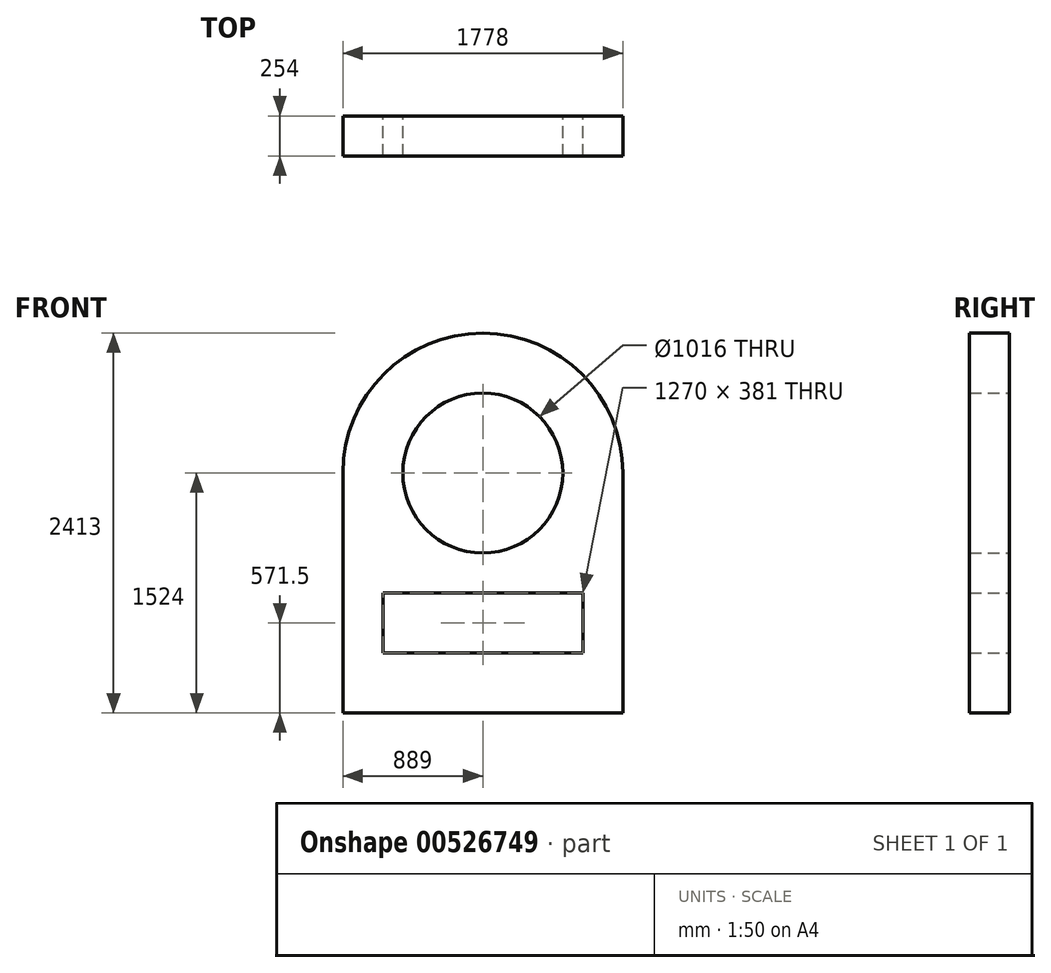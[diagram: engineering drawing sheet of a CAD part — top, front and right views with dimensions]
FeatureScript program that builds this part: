
annotation { "Feature Type Name" : "Feature", "Feature Type Description" : "" }
export const myFeature = defineFeature(function(context is Context, id is Id, definition is map)
    precondition{}
    {
        {
            var Q0;
            Q0=qCreatedBy(makeId("Front.planeOp"),FACE);
            var sketch = newSketch(context, id + "F0", { "sketchPlane" : qUnion([Q0])});
            skLineSegment(sketch, "E0", {"start": v(0, 0) * mm, "end": v(1778, 0) * mm});
            skLineSegment(sketch, "E1", {"start": v(1778, 0) * mm, "end": v(1778, 1524) * mm});
            skLineSegment(sketch, "E2", {"start": v(0, 1524) * mm, "end": v(0, 0) * mm});
            skLineSegment(sketch, "E3", {"start": v(254, 762) * mm, "end": v(254, 381) * mm});
            skLineSegment(sketch, "E4", {"start": v(254, 381) * mm, "end": v(1524, 381) * mm});
            skLineSegment(sketch, "E5", {"start": v(1524, 381) * mm, "end": v(1524, 762) * mm});
            skLineSegment(sketch, "E6", {"start": v(1524, 762) * mm, "end": v(254, 762) * mm});
            skArc(sketch, "E7", {"start": v(1778, 1524) * mm, "mid": v(889, 2413) * mm, "end": v(0, 1524) * mm});
            skCircle(sketch, "E8", {"center": v(889, 1524) * mm, "radius": 508 * mm});
            skSolve(sketch);
        }
        {
            var Q0;
            Q0 = qSketchRegion(id + "F0", true);
            var Q1;
            Q1=makeQuery(id+"F0.imprint","IMPRINT",FACE,{"disambiguationData":[TD([[makeQuery(id+"F0.imprint","IMPRINT",EDGE,{"derivedFrom":sQuery(id+"F0.wireOp",EDGE,"E0")}),1.0]])]});
            extrude(context, id + "F1", {"entities" : qUnion([Q0, Q1]), "depth" : 254 * mm, "offsetDistance" : 25.4 * mm});
        }
    });
